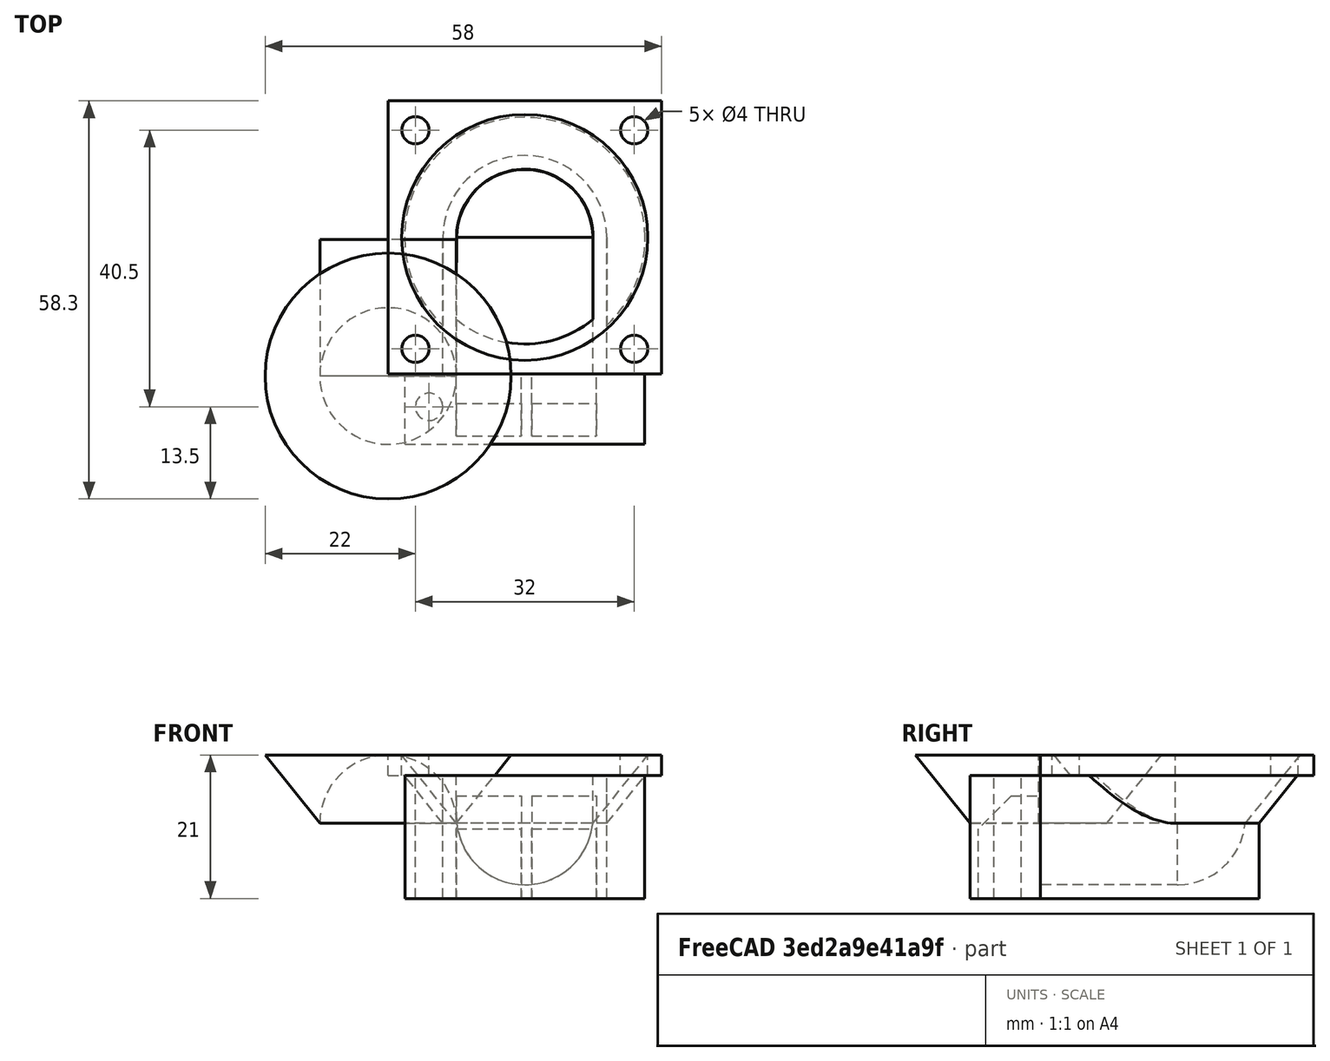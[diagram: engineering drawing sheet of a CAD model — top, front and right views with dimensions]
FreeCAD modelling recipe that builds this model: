
FCSTD DOCUMENT  (FreeCAD 0.16R6712 (Git))
Label: E3DV6_4040FanDuct
License: All rights reserved
LicenseURL: http://en.wikipedia.org/wiki/All_rights_reserved
objects: Part::Box×7, Part::MultiFuse×7, Part::Cylinder×7, Part::Cut×5, Part::Cone×3, Part::Sphere×1, Part::Feature×1
note: 31 computed .brp shape members not serialized (recipe doc carries the construction recipe); baked Part::Feature solids carry a one-line shape summary decoded from their .brp

FEATURE [Part::Box] Box  label="Würfel"
  Height = 3
  Length = 40
  Placement = pos=(0,0,7) rot=(0,0,1;0rad)
  Width = 40
FEATURE [Part::Cone] Cone  label="Kegel"
  Angle = 360
  Height = 10
  Placement = pos=(20,20,0) rot=(0,0,1;0rad)
  Radius1 = 10
  Radius2 = 18
FEATURE [Part::Cone] Cone001  label="Kegel001"
  Angle = 360
  Height = 10
  Placement = pos=(20,20,0) rot=(0,0,1;0rad)
  Radius1 = 12
  Radius2 = 20
FEATURE [Part::Box] Box001  label="Würfel001"
  Height = 18
  Length = 35
  Placement = pos=(2.5,-10,-11) rot=(0,0,1;0rad)
  Width = 10.3
FEATURE [Part::MultiFuse] Fusion
  Shapes = -> [Cone001,Box]
FEATURE [Part::Box] Box002  label="Würfel002"
  Height = 6
  Length = 20
  Placement = pos=(10,0,1) rot=(0,0,1;0rad)
  Width = 20
FEATURE [Part::Box] Box003  label="Würfel003"
  Height = 18
  Length = 24
  Placement = pos=(8,0,-11) rot=(0,0,1;0rad)
  Width = 20
FEATURE [Part::Cylinder] Cylinder001  label="Zylinder001"
  Angle = 360
  Height = 12
  Placement = pos=(20,20,-11) rot=(0,0,1;0rad)
  Radius = 12
FEATURE [Part::MultiFuse] Fusion003  label="aussen"
  Shapes = -> [Box003,Cylinder001]
FEATURE [Part::Cone] Cone002  label="Kegel002"
  Angle = 360
  Height = 10
  Radius1 = 10
  Radius2 = 18
FEATURE [Part::Sphere] Sphere  label="Kugel"
  Angle1 = -90
  Angle2 = 90
  Angle3 = 360
  Placement = pos=(20,20,1) rot=(1,0,0;0.017453rad)
  Radius = 10
FEATURE [Part::Cylinder] Cylinder  label="Zylinder"
  Angle = 180
  Height = 20
  Placement = pos=(0,20,0) rot=(1,0,0;1.5708rad)
  Radius = 10
FEATURE [Part::Feature] Cylinder002  label="Zylinder002"
  Placement = pos=(20,0,1) rot=(0,1,0;3.14159rad)
  shape: bbox 20 x 20 x 10 mm, 4 faces (baked)
FEATURE [Part::MultiFuse] Fusion004  label="inner"
  Shapes = -> [Cylinder002,Box002,Sphere]
FEATURE [Part::MultiFuse] Fusion005  label="Hohlraum"
  Shapes = -> [Cone,Fusion004]
FEATURE [Part::MultiFuse] Fusion006  label="Wall"
  Shapes = -> [Fusion,Fusion003]
FEATURE [Part::Cut] Cut
  Base = -> Fusion006
  Placement = pos=(0,0.3,0) rot=(0,0,1;0rad)
  Tool = -> Fusion005
FEATURE [Part::Box] Box004  label="Würfel004"
  Height = 15
  Length = 9.5
  Placement = pos=(10,-8.8,-11) rot=(0,0,1;0rad)
  Width = 10
FEATURE [Part::Box] Box006  label="Würfel006"
  Height = 15
  Length = 9.5
  Placement = pos=(21,-8.8,-11) rot=(0,0,1;0rad)
  Width = 10
FEATURE [Part::MultiFuse] Fusion007
  Shapes = -> [Box004,Box006]
FEATURE [Part::Cylinder] Cylinder003  label="Zylinder003"
  Angle = 360
  Height = 20
  Placement = pos=(6,-4.5,-12) rot=(0,0,1;0rad)
  Radius = 2
FEATURE [Part::Box] Box007  label="Würfel007"
  Height = 10
  Length = 36
  Placement = pos=(0,-10,-2) rot=(1,0,0;0.785398rad)
  Width = 10
FEATURE [Part::Cut] Cut001
  Base = -> Fusion007
  Tool = -> Box007
FEATURE [Part::Cut] Cut002
  Base = -> Box001
  Tool = -> Cut001
FEATURE [Part::Cut] Cut003
  Base = -> Cut002
  Tool = -> Cylinder003
FEATURE [Part::Cylinder] Cylinder004  label="Zylinder004"
  Angle = 360
  Height = 10
  Radius = 2
FEATURE [Part::Cylinder] Cylinder005  label="Zylinder005"
  Angle = 360
  Height = 10
  Placement = pos=(0,32,0) rot=(0,0,1;0rad)
  Radius = 2
FEATURE [Part::Cylinder] Cylinder006  label="Zylinder006"
  Angle = 360
  Height = 10
  Placement = pos=(32,0,0) rot=(0,0,1;0rad)
  Radius = 2
FEATURE [Part::Cylinder] Cylinder007  label="Zylinder007"
  Angle = 360
  Height = 10
  Placement = pos=(32,32,0) rot=(0,0,1;0rad)
  Radius = 2
FEATURE [Part::MultiFuse] Fusion008  label="LüfterBohrung"
  Placement = pos=(4,4,0) rot=(0,0,1;0rad)
  Shapes = -> [Cylinder004,Cylinder005,Cylinder007,Cylinder006]
FEATURE [Part::Cut] Cut004
  Base = -> Cut
  Tool = -> Fusion008
